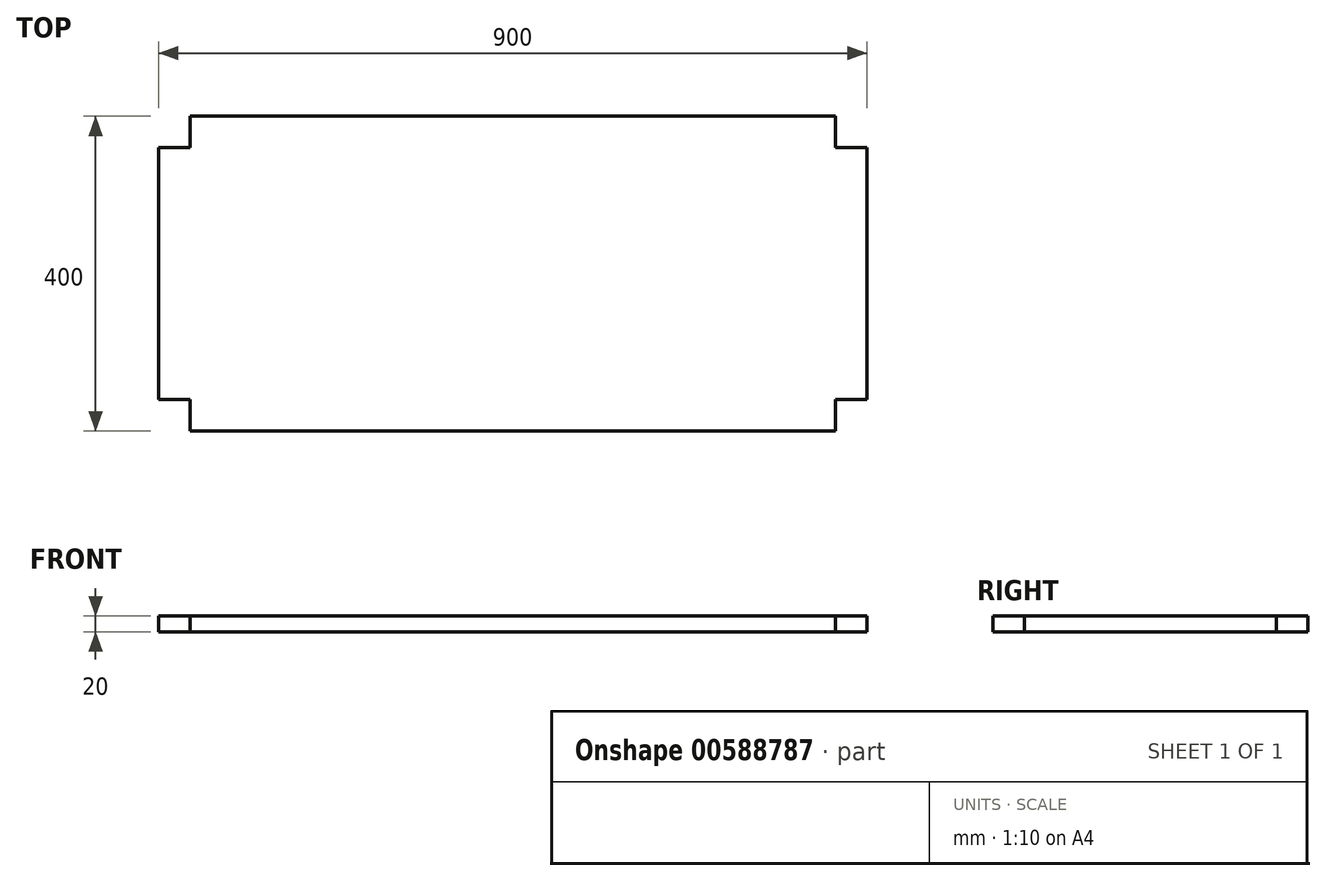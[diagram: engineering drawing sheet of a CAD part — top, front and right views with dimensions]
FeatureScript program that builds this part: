
annotation { "Feature Type Name" : "Feature", "Feature Type Description" : "" }
export const myFeature = defineFeature(function(context is Context, id is Id, definition is map)
    precondition{}
    {
        {
            var Q0;
            Q0=qCreatedBy(makeId("Top.planeOp"),FACE);
            var sketch = newSketch(context, id + "F0", { "sketchPlane" : qUnion([Q0])});
            skLineSegment(sketch, "E0", {"start": v(-62.08, -40) * mm, "end": v(-62.08, 0) * mm});
            skLineSegment(sketch, "E1", {"start": v(-62.08, 0) * mm, "end": v(-102.08, 0) * mm});
            skLineSegment(sketch, "E2", {"start": v(-102.08, 0) * mm, "end": v(-102.08, 320) * mm});
            skLineSegment(sketch, "E3", {"start": v(-102.08, 320) * mm, "end": v(-62.08, 320) * mm});
            skLineSegment(sketch, "E4", {"start": v(-62.08, 320) * mm, "end": v(-62.08, 360) * mm});
            skLineSegment(sketch, "E5", {"start": v(-62.08, 360) * mm, "end": v(757.92, 360) * mm});
            skLineSegment(sketch, "E6", {"start": v(757.92, 320) * mm, "end": v(757.92, 360) * mm});
            skLineSegment(sketch, "E7", {"start": v(757.92, 320) * mm, "end": v(797.92, 320) * mm});
            skLineSegment(sketch, "E8", {"start": v(797.92, 320) * mm, "end": v(797.92, 0) * mm});
            skLineSegment(sketch, "E9", {"start": v(797.92, 0) * mm, "end": v(757.92, 0) * mm});
            skLineSegment(sketch, "E10", {"start": v(757.92, 0) * mm, "end": v(757.92, -40) * mm});
            skLineSegment(sketch, "E11", {"start": v(757.92, -40) * mm, "end": v(-62.08, -40) * mm});
            skSolve(sketch);
        }
        {
            var Q0;
            Q0=makeQuery(id+"F0.imprint","IMPRINT",FACE,{"disambiguationData":[TD([[makeQuery(id+"F0.imprint","IMPRINT",EDGE,{"derivedFrom":sQuery(id+"F0.wireOp",EDGE,"E0")}),-1.0]])]});
            extrude(context, id + "F1", {"entities" : qUnion([Q0]), "depth" : 20 * mm, "offsetDistance" : 25 * mm});
        }
    });
